# Revit family: Drain_Top_Adjustable_8_Inch-Zurn-Z556-Heavy-Duty
name_source: partatom
category: Plumbing Fixtures
units: mm (PartAtom-declared; Revit-internal decimal feet)

## family parameters
Always vertical = Yes
Cut with Voids When Loaded = No
Maintain Annotation Orientation = No
OmniClass Number = 23.45.55.21
OmniClass Title = Drains (Wastes)
Part Type = Normal
Room Calculation Point = No
Round Connector Dimension = Use Radius
Shared = No
Work Plane-Based = No

## types (18) — shared parameters
Approx. Weight (Lbs) = 60 "
Assembly Code = D2030300
CW Connection = No
Default Elevation = 25 "
Description = 12-1/4 [311] DIAMETER TOP ADJUSTABLE HEAVY-DUTY DRAIN
Grate Open Area Sq.in = 33 "
HW Connection = No
Main Material = Iron - Zurn - Cast - Painted - Blue
Manufacturer = Zurn Water, LLC
Manufacurer Brand = Zurn
Modified Date = 12/19/2025
Product Documentation Link = https://files.zurn.com
Product Page URL = https://www.zurn.com
Product data url = https://www.bimobject.com
Top inner Diameter = 8 "
URL = www.zurn.com
Vent Connection = No
WFU = 1
Waste Connection = Yes
Width = 8.375 "
zero-valued in all types: CWFU, HWFU

## per-type parameters (varying)
| type | A_ Pipe Size (Actual-Inner) | A_ Pipe Size (Actual-Outer) | A_ Pipe Size (Nominal) | Body Height_E | Connector Radius | Frame and Grate | Model | Type Comments | ZN-Frame Height | ZN-Top |
| Z556-2IP | 2.067 " | 2.375 " | 2 " | 2.625 " | 1 " | Iron - Zurn - Cast - Painted - Blue | Z556 | Z556-2 Inch-Threaded Outlet | 0 " | No |
| Z556-2NH | 2.067 " | 2.375 " | 2 " | 3.875 " | 1 " | Iron - Zurn - Cast - Painted - Blue | Z556 | Z556-2 Inch-No Hub Outlet | 0 " | No |
| Z556-2NL | 2.067 " | 2.375 " | 2 " | 3.75 " | 1 " | Iron - Zurn - Cast - Painted - Blue | Z556 | Z556-2 Inch-Neo Loc Outlet | 0 " | No |
| Z556-3IP | 3.068 " | 3.5 " | 3 " | 2.625 " | 1.5 " | Iron - Zurn - Cast - Painted - Blue | Z556 | Z556-3 Inch-Threaded Outlet | 0 " | No |
| Z556-3NH | 3.068 " | 3.5 " | 3 " | 3.875 " | 1.5 " | Iron - Zurn - Cast - Painted - Blue | Z556 | Z556-3 Inch-No Hub Outlet | 0 " | No |
| Z556-3NL | 3.068 " | 3.5 " | 3 " | 3.75 " | 1.5 " | Iron - Zurn - Cast - Painted - Blue | Z556 | Z556-3 Inch-Neo Loc Outlet | 0 " | No |
| Z556-4IP | 4.026 " | 4.5 " | 4 " | 2.625 " | 2 " | Iron - Zurn - Cast - Painted - Blue | Z556 | Z556-4 Inch-Threaded Outlet | 0 " | No |
| Z556-4NH | 4.026 " | 4.5 " | 4 " | 3.875 " | 2 " | Iron - Zurn - Cast - Painted - Blue | Z556 | Z556-4 Inch-No Hub Outlet | 0 " | No |
| Z556-4NL | 4.026 " | 4.5 " | 4 " | 3.75 " | 2 " | Iron - Zurn - Cast - Painted - Blue | Z556 | Z556-4 Inch-Neo Loc Outlet | 0 " | No |
| ZN556-2IP | 2.067 " | 2.375 " | 2 " | 2.625 " | 1 " | Bronze - Zurn - Polished Nickel | ZN556 | ZN556-2 Inch-Threaded Outlet | 0.188 " | Yes |
| ZN556-2NH | 2.067 " | 2.375 " | 2 " | 3.875 " | 1 " | Bronze - Zurn - Polished Nickel | ZN556 | ZN556-2 Inch-No Hub Outlet | 0.188 " | Yes |
| ZN556-2NL | 2.067 " | 2.375 " | 2 " | 3.75 " | 1 " | Bronze - Zurn - Polished Nickel | ZN556 | ZN556-2 Inch-Neo Loc Outlet | 0.188 " | Yes |
| ZN556-3IP | 3.068 " | 3.5 " | 3 " | 2.625 " | 1.5 " | Bronze - Zurn - Polished Nickel | ZN556 | ZN556-3 Inch-Threaded Outlet | 0.188 " | Yes |
| ZN556-3NH | 3.068 " | 3.5 " | 3 " | 3.875 " | 1.5 " | Bronze - Zurn - Polished Nickel | ZN556 | ZN556-3 Inch-No Hub Outlet | 0.188 " | Yes |
| ZN556-3NL | 3.068 " | 3.5 " | 3 " | 3.75 " | 1.5 " | Bronze - Zurn - Polished Nickel | ZN556 | ZN556-3 Inch-Neo Loc Outlet | 0.188 " | Yes |
| ZN556-4IP | 4.026 " | 4.5 " | 4 " | 2.625 " | 2 " | Bronze - Zurn - Polished Nickel | ZN556 | ZN556-4 Inch-Threaded Outlet | 0.188 " | Yes |
| ZN556-4NH | 4.026 " | 4.5 " | 4 " | 3.875 " | 2 " | Bronze - Zurn - Polished Nickel | ZN556 | ZN556-4 Inch-No Hub Outlet | 0.188 " | Yes |
| ZN556-4NL | 4.026 " | 4.5 " | 4 " | 3.75 " | 2 " | Bronze - Zurn - Polished Nickel | ZN556 | ZN556-4 Inch-Neo Loc Outlet | 0.188 " | Yes |

## geometry (parser evidence)
native form markers: Sweep x4
no freeform markers — native parametric forms only
